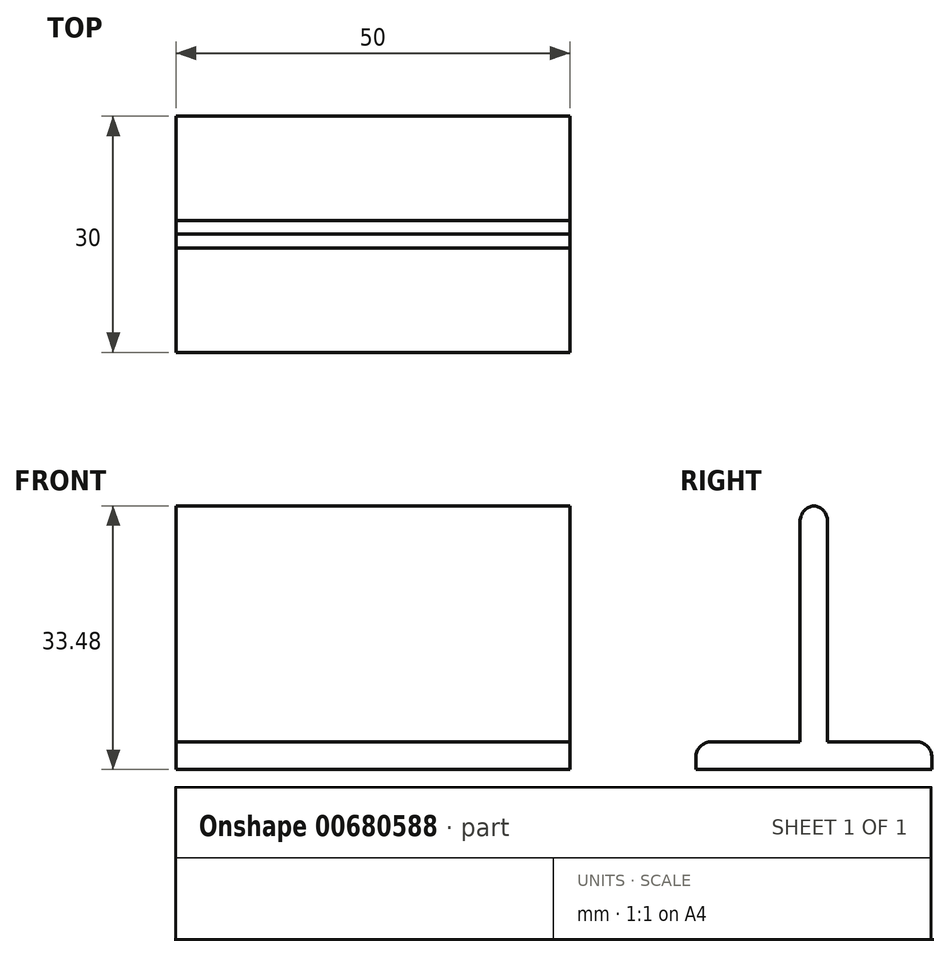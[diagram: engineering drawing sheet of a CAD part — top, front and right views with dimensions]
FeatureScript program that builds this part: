
annotation { "Feature Type Name" : "Feature", "Feature Type Description" : "" }
export const myFeature = defineFeature(function(context is Context, id is Id, definition is map)
    precondition{}
    {
        {
            var Q0;
            Q0=qCreatedBy(makeId("Top.planeOp"),FACE);
            var sketch = newSketch(context, id + "F0", { "sketchPlane" : qUnion([Q0])});
            skLineSegment(sketch, "E0.bottom", {"start": v(25, 15) * mm, "end": v(-25, 15) * mm});
            skLineSegment(sketch, "E0.top", {"start": v(25, -15) * mm, "end": v(-25, -15) * mm});
            skLineSegment(sketch, "E0.left", {"start": v(25, 15) * mm, "end": v(25, -15) * mm});
            skLineSegment(sketch, "E0.right", {"start": v(-25, 15) * mm, "end": v(-25, -15) * mm});
            skPoint(sketch, "E0.middle", {"position": v(0, 0) * mm});
            skSolve(sketch);
        }
        {
            var Q0;
            Q0=makeQuery(id+"F0.imprint","IMPRINT",FACE,{"disambiguationData":[TD([[makeQuery(id+"F0.imprint","IMPRINT",EDGE,{"derivedFrom":sQuery(id+"F0.wireOp",EDGE,"E0.bottom")}),1.0]])]});
            extrude(context, id + "F1", {"entities" : qUnion([Q0]), "depth" : 3.5 * mm, "offsetDistance" : 25 * mm});
        }
        {
            var Q0;
            Q0=makeQuery(id+"F1.opExtrude","CAP_EDGE",EDGE,{"disambiguationData":[OSD([sQuery(id+"F0.wireOp",EDGE,"E0.bottom")])],"isStart":false});
            var Q1;
            Q1=makeQuery(id+"F1.opExtrude","CAP_EDGE",EDGE,{"disambiguationData":[OSD([sQuery(id+"F0.wireOp",EDGE,"E0.top")])],"isStart":false});
            fillet(context, id + "F2", {"entities" : qUnion([Q0, Q1]), "radius" : 2 * mm, "tangentPropagation" : true, "allowEdgeOverflow" : false});
        }
        {
            var Q0;
            Q0=makeQuery(id+"F1.opExtrude","CAP_FACE",FACE,{"disambiguationData":[OSD([sQuery(id+"F0.wireOp",EDGE,"E0.bottom"),sQuery(id+"F0.wireOp",EDGE,"E0.top"),sQuery(id+"F0.wireOp",EDGE,"E0.left"),sQuery(id+"F0.wireOp",EDGE,"E0.right")])],"isStart":false});
            var sketch = newSketch(context, id + "F3", { "sketchPlane" : qUnion([Q0])});
            skLineSegment(sketch, "E1", {"start": v(-25, -1.75) * mm, "end": v(25, -1.75) * mm});
            skLineSegment(sketch, "E2", {"start": v(25, -1.75) * mm, "end": v(25, 1.75) * mm});
            skLineSegment(sketch, "E3", {"start": v(25, 1.75) * mm, "end": v(-25, 1.75) * mm});
            skLineSegment(sketch, "E4", {"start": v(-25, 1.75) * mm, "end": v(-25, -1.75) * mm});
            skSolve(sketch);
        }
        {
            var Q0;
            Q0=makeQuery(id+"F3.imprint","IMPRINT",FACE,{"disambiguationData":[TD([[makeQuery(id+"F3.imprint","IMPRINT",EDGE,{"derivedFrom":sQuery(id+"F3.wireOp",EDGE,"E1")}),1.0]])]});
            extrude(context, id + "F4", {"entities" : qUnion([Q0]), "operationType" : NewBodyOperationType.ADD, "depth" : 30 * mm, "offsetDistance" : 25 * mm});
        }
        {
            var Q0;
            Q0=makeQuery(id+"F4.opExtrude","CAP_EDGE",EDGE,{"disambiguationData":[OSD([sQuery(id+"F3.wireOp",EDGE,"E1")])],"isStart":false});
            var Q1;
            Q1=makeQuery(id+"F4.opExtrude","CAP_EDGE",EDGE,{"disambiguationData":[OSD([sQuery(id+"F3.wireOp",EDGE,"E3")])],"isStart":false});
            fillet(context, id + "F5", {"entities" : qUnion([Q0, Q1]), "radius" : 2 * mm, "tangentPropagation" : true, "allowEdgeOverflow" : false});
        }
    });
